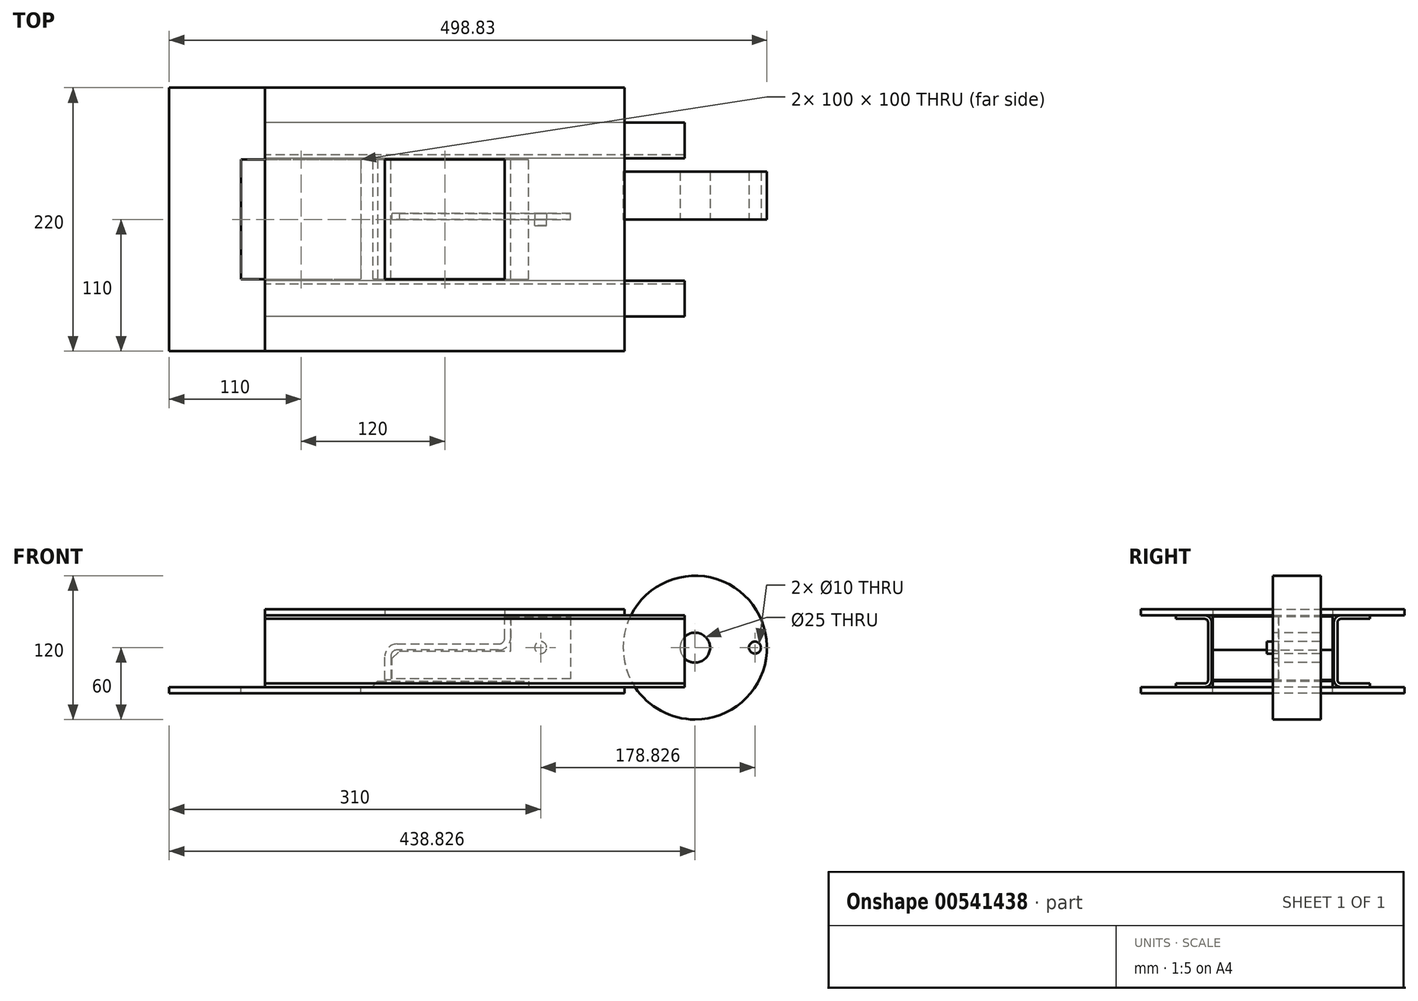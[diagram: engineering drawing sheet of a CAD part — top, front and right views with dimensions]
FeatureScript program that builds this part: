
annotation { "Feature Type Name" : "Feature", "Feature Type Description" : "" }
export const myFeature = defineFeature(function(context is Context, id is Id, definition is map)
    precondition{}
    {
        {
            var Q0;
            Q0=qCreatedBy(makeId("Top.planeOp"),FACE);
            var sketch = newSketch(context, id + "F0", { "sketchPlane" : qUnion([Q0])});
            skLineSegment(sketch, "E0.bottom", {"start": v(-50, -50) * mm, "end": v(50, -50) * mm});
            skLineSegment(sketch, "E0.top", {"start": v(-50, 50) * mm, "end": v(50, 50) * mm});
            skLineSegment(sketch, "E0.left", {"start": v(-50, -50) * mm, "end": v(-50, 50) * mm});
            skLineSegment(sketch, "E0.right", {"start": v(50, -50) * mm, "end": v(50, 50) * mm});
            skLineSegment(sketch, "E1.bottom", {"start": v(-150, -110) * mm, "end": v(150, -110) * mm});
            skLineSegment(sketch, "E1.top", {"start": v(-150, 110) * mm, "end": v(150, 110) * mm});
            skLineSegment(sketch, "E1.left", {"start": v(-150, -110) * mm, "end": v(-150, 110) * mm});
            skLineSegment(sketch, "E1.right", {"start": v(150, -110) * mm, "end": v(150, 110) * mm});
            skSolve(sketch);
        }
        {
            var Q0;
            Q0=makeQuery(id+"F0.imprint","IMPRINT",FACE,{"disambiguationData":[TD([[makeQuery(id+"F0.imprint","IMPRINT",EDGE,{"derivedFrom":sQuery(id+"F0.wireOp",EDGE,"E0.bottom")}),-1.0]])]});
            extrude(context, id + "F1", {"entities" : qUnion([Q0]), "depth" : 5 * mm, "offsetDistance" : 25 * mm});
        }
        {
            var Q0;
            Q0=makeQuery(id+"F1.opExtrude","CAP_FACE",FACE,{"disambiguationData":[OSD([sQuery(id+"F0.wireOp",EDGE,"E0.bottom"),sQuery(id+"F0.wireOp",EDGE,"E0.top"),sQuery(id+"F0.wireOp",EDGE,"E0.left"),sQuery(id+"F0.wireOp",EDGE,"E0.right"),sQuery(id+"F0.wireOp",EDGE,"E1.bottom"),sQuery(id+"F0.wireOp",EDGE,"E1.top"),sQuery(id+"F0.wireOp",EDGE,"E1.left"),sQuery(id+"F0.wireOp",EDGE,"E1.right")])],"isStart":true});
            cPlane(context, id + "F2", {"entities" : qUnion([Q0]), "cplaneType" : CPlaneType.OFFSET, "offset" : 60 * mm, "width" : 150 * mm, "height" : 150 * mm});
        }
        {
            var Q0;
            Q0=qCreatedBy(id+"F2.planeOp",FACE);
            var sketch = newSketch(context, id + "F3", { "sketchPlane" : qUnion([Q0])});
            skLineSegment(sketch, "E2.bottom", {"start": v(-170, -50) * mm, "end": v(-70, -50) * mm});
            skLineSegment(sketch, "E2.top", {"start": v(-170, 50) * mm, "end": v(-70, 50) * mm});
            skLineSegment(sketch, "E2.left", {"start": v(-170, -50) * mm, "end": v(-170, 50) * mm});
            skLineSegment(sketch, "E2.right", {"start": v(-70, -50) * mm, "end": v(-70, 50) * mm});
            skLineSegment(sketch, "E3.bottom", {"start": v(-230, -110) * mm, "end": v(150, -110) * mm});
            skLineSegment(sketch, "E3.top", {"start": v(-230, 110) * mm, "end": v(150, 110) * mm});
            skLineSegment(sketch, "E3.left", {"start": v(-230, -110) * mm, "end": v(-230, 110) * mm});
            skLineSegment(sketch, "E3.right", {"start": v(150, -110) * mm, "end": v(150, 110) * mm});
            skSolve(sketch);
        }
        {
            var Q0;
            Q0=makeQuery(id+"F3.imprint","IMPRINT",FACE,{"disambiguationData":[TD([[makeQuery(id+"F3.imprint","IMPRINT",EDGE,{"derivedFrom":sQuery(id+"F3.wireOp",EDGE,"E2.bottom")}),-1.0]])]});
            extrude(context, id + "F4", {"entities" : qUnion([Q0]), "depth" : 5 * mm, "offsetDistance" : 25 * mm});
        }
        {
            var Q0;
            Q0=qCreatedBy(makeId("Front.planeOp"),FACE);
            var sketch = newSketch(context, id + "F5", { "sketchPlane" : qUnion([Q0])});
            skLineSegment(sketch, "E4", {"start": v(-50, -54) * mm, "end": v(-50, -24) * mm});
            skLineSegment(sketch, "E5", {"start": v(-50, -24) * mm, "end": v(50, -24) * mm});
            skLineSegment(sketch, "E6", {"start": v(50, -24) * mm, "end": v(50, -1) * mm});
            skLineSegment(sketch, "E7", {"start": v(50, -1) * mm, "end": v(55, -1) * mm});
            skLineSegment(sketch, "E8", {"start": v(55, -1) * mm, "end": v(55, -29) * mm});
            skLineSegment(sketch, "E9", {"start": v(55, -29) * mm, "end": v(-45, -29) * mm});
            skLineSegment(sketch, "E10", {"start": v(-45, -29) * mm, "end": v(-45, -54) * mm});
            skLineSegment(sketch, "E11", {"start": v(-45, -54) * mm, "end": v(-50, -54) * mm});
            skSolve(sketch);
        }
        {
            var Q0;
            Q0=makeQuery(id+"F5.imprint","IMPRINT",FACE,{"disambiguationData":[TD([[makeQuery(id+"F5.imprint","IMPRINT",EDGE,{"derivedFrom":sQuery(id+"F5.wireOp",EDGE,"E4")}),-1.0]])]});
            extrude(context, id + "F6", {"entities" : qUnion([Q0]), "endBound" : BoundingType.SYMMETRIC, "depth" : 100 * mm, "offsetDistance" : 25 * mm});
        }
        {
            var Q0;
            Q0=makeQuery(id+"F6.opExtrude","SWEPT_EDGE",EDGE,{"disambiguationData":[OSD([sQuery(id+"F5.wireOp",EDGE,"E4"),sQuery(id+"F5.wireOp",EDGE,"E5")])]});
            var Q1;
            Q1=makeQuery(id+"F6.opExtrude","SWEPT_EDGE",EDGE,{"disambiguationData":[OSD([sQuery(id+"F5.wireOp",EDGE,"E8"),sQuery(id+"F5.wireOp",EDGE,"E9")])]});
            fillet(context, id + "F7", {"entities" : qUnion([Q0, Q1]), "radius" : 10 * mm, "tangentPropagation" : true, "allowEdgeOverflow" : false});
        }
        {
            var Q0;
            Q0=makeQuery(id+"F6.opExtrude","SWEPT_EDGE",EDGE,{"disambiguationData":[OSD([sQuery(id+"F5.wireOp",EDGE,"E9"),sQuery(id+"F5.wireOp",EDGE,"E10")])]});
            var Q1;
            Q1=makeQuery(id+"F6.opExtrude","SWEPT_EDGE",EDGE,{"disambiguationData":[OSD([sQuery(id+"F5.wireOp",EDGE,"E5"),sQuery(id+"F5.wireOp",EDGE,"E6")])]});
            fillet(context, id + "F8", {"entities" : qUnion([Q0, Q1]), "radius" : 5 * mm, "tangentPropagation" : true, "allowEdgeOverflow" : false});
        }
        {
            var Q0;
            Q0=qCreatedBy(id+"F2.planeOp",FACE);
            var sketch = newSketch(context, id + "F9", { "sketchPlane" : qUnion([Q0])});
            skLineSegment(sketch, "E12.bottom", {"start": v(-60, 50) * mm, "end": v(70, 50) * mm});
            skLineSegment(sketch, "E12.top", {"start": v(-60, -50) * mm, "end": v(70, -50) * mm});
            skLineSegment(sketch, "E12.left", {"start": v(-60, 50) * mm, "end": v(-60, -50) * mm});
            skLineSegment(sketch, "E12.right", {"start": v(70, 50) * mm, "end": v(70, -50) * mm});
            skSolve(sketch);
        }
        {
            var Q0;
            Q0=makeQuery(id+"F9.imprint","IMPRINT",FACE,{"disambiguationData":[TD([[makeQuery(id+"F9.imprint","IMPRINT",EDGE,{"derivedFrom":sQuery(id+"F9.wireOp",EDGE,"E12.bottom")}),-1.0]])]});
            extrude(context, id + "F10", {"entities" : qUnion([Q0]), "oppositeDirection" : true, "depth" : 5 * mm, "offsetDistance" : 25 * mm});
        }
        {
            var Q0;
            Q0=makeQuery(id+"F10.opExtrude","CAP_EDGE",EDGE,{"disambiguationData":[OSD([sQuery(id+"F9.wireOp",EDGE,"E12.left")])],"isStart":false});
            chamfer(context, id + "F11", {"entities" : qUnion([Q0]), "width" : 4 * mm, "tangentPropagation" : true});
        }
        {
            var Q0;
            Q0=qCreatedBy(makeId("Right.planeOp"),FACE);
            var sketch = newSketch(context, id + "F12", { "sketchPlane" : qUnion([Q0])});
            skLineSegment(sketch, "E13", {"start": v(-81, 0) * mm, "end": v(-51, 0) * mm});
            skLineSegment(sketch, "E14", {"start": v(-51, 0) * mm, "end": v(-51, -60) * mm});
            skLineSegment(sketch, "E15", {"start": v(-51, -60) * mm, "end": v(-81, -60) * mm});
            skLineSegment(sketch, "E16", {"start": v(-81, -60) * mm, "end": v(-81, -57) * mm});
            skLineSegment(sketch, "E17", {"start": v(-81, -57) * mm, "end": v(-54, -57) * mm});
            skLineSegment(sketch, "E18", {"start": v(-54, -57) * mm, "end": v(-54, -3) * mm});
            skLineSegment(sketch, "E19", {"start": v(-54, -3) * mm, "end": v(-81, -3) * mm});
            skLineSegment(sketch, "E20", {"start": v(-81, -3) * mm, "end": v(-81, 0) * mm});
            skSolve(sketch);
        }
        {
            var Q0;
            Q0=makeQuery(id+"F12.imprint","IMPRINT",FACE,{"disambiguationData":[TD([[makeQuery(id+"F12.imprint","IMPRINT",EDGE,{"derivedFrom":sQuery(id+"F12.wireOp",EDGE,"E13")}),-1.0]])]});
            extrude(context, id + "F13", {"entities" : qUnion([Q0]), "endBound" : BoundingType.SYMMETRIC, "depth" : 350 * mm, "offsetDistance" : 25 * mm});
        }
        {
            var Q0;
            Q0=makeQuery(id+"F13.opExtrude","SWEPT_BODY",BODY,{"disambiguationData":[OSD([sQuery(id+"F12.wireOp",EDGE,"E13"),sQuery(id+"F12.wireOp",EDGE,"E14"),sQuery(id+"F12.wireOp",EDGE,"E15"),sQuery(id+"F12.wireOp",EDGE,"E16"),sQuery(id+"F12.wireOp",EDGE,"E17"),sQuery(id+"F12.wireOp",EDGE,"E18"),sQuery(id+"F12.wireOp",EDGE,"E19"),sQuery(id+"F12.wireOp",EDGE,"E20")])]});
            var Q1;
            Q1=qCreatedBy(makeId("Front.planeOp"),FACE);
            mirror(context, id + "F14", {"entities" : qUnion([Q0]), "mirrorPlane" : qUnion([Q1])});
        }
        {
            var Q0;
            Q0=makeQuery(id+"F13.opExtrude","SWEPT_EDGE",EDGE,{"disambiguationData":[OSD([sQuery(id+"F12.wireOp",EDGE,"E18"),sQuery(id+"F12.wireOp",EDGE,"E19")])]});
            var Q1;
            Q1=makeQuery(id+"F13.opExtrude","SWEPT_EDGE",EDGE,{"disambiguationData":[OSD([sQuery(id+"F12.wireOp",EDGE,"E17"),sQuery(id+"F12.wireOp",EDGE,"E18")])]});
            var Q2;
            Q2=makeQuery(id+"F14.opPattern","COPY",EDGE,{"derivedFrom":makeQuery(id+"F13.opExtrude","SWEPT_EDGE",EDGE,{"disambiguationData":[OSD([sQuery(id+"F12.wireOp",EDGE,"E17"),sQuery(id+"F12.wireOp",EDGE,"E18")])]}),"instanceName":"1"});
            var Q3;
            Q3=makeQuery(id+"F14.opPattern","COPY",EDGE,{"derivedFrom":makeQuery(id+"F13.opExtrude","SWEPT_EDGE",EDGE,{"disambiguationData":[OSD([sQuery(id+"F12.wireOp",EDGE,"E18"),sQuery(id+"F12.wireOp",EDGE,"E19")])]}),"instanceName":"1"});
            fillet(context, id + "F15", {"entities" : qUnion([Q0, Q1, Q2, Q3]), "radius" : 3 * mm, "tangentPropagation" : true, "allowEdgeOverflow" : false});
        }
        {
            var Q0;
            Q0=makeQuery(id+"F13.opExtrude","SWEPT_EDGE",EDGE,{"disambiguationData":[OSD([sQuery(id+"F12.wireOp",EDGE,"E13"),sQuery(id+"F12.wireOp",EDGE,"E14")])]});
            var Q1;
            Q1=makeQuery(id+"F13.opExtrude","SWEPT_EDGE",EDGE,{"disambiguationData":[OSD([sQuery(id+"F12.wireOp",EDGE,"E14"),sQuery(id+"F12.wireOp",EDGE,"E15")])]});
            var Q2;
            Q2=makeQuery(id+"F14.opPattern","COPY",EDGE,{"derivedFrom":makeQuery(id+"F13.opExtrude","SWEPT_EDGE",EDGE,{"disambiguationData":[OSD([sQuery(id+"F12.wireOp",EDGE,"E13"),sQuery(id+"F12.wireOp",EDGE,"E14")])]}),"instanceName":"1"});
            var Q3;
            Q3=makeQuery(id+"F14.opPattern","COPY",EDGE,{"derivedFrom":makeQuery(id+"F13.opExtrude","SWEPT_EDGE",EDGE,{"disambiguationData":[OSD([sQuery(id+"F12.wireOp",EDGE,"E14"),sQuery(id+"F12.wireOp",EDGE,"E15")])]}),"instanceName":"1"});
            fillet(context, id + "F16", {"entities" : qUnion([Q0, Q1, Q2, Q3]), "radius" : 6 * mm, "tangentPropagation" : true, "allowEdgeOverflow" : false});
        }
        {
            var Q0;
            Q0=makeQuery(id+"F14.opPattern","COPY",BODY,{"derivedFrom":makeQuery(id+"F13.opExtrude","SWEPT_BODY",BODY,{"disambiguationData":[OSD([sQuery(id+"F12.wireOp",EDGE,"E13"),sQuery(id+"F12.wireOp",EDGE,"E14"),sQuery(id+"F12.wireOp",EDGE,"E15"),sQuery(id+"F12.wireOp",EDGE,"E16"),sQuery(id+"F12.wireOp",EDGE,"E17"),sQuery(id+"F12.wireOp",EDGE,"E18"),sQuery(id+"F12.wireOp",EDGE,"E19"),sQuery(id+"F12.wireOp",EDGE,"E20")])]}),"instanceName":"1"});
            var Q1;
            Q1=makeQuery(id+"F13.opExtrude","SWEPT_BODY",BODY,{"disambiguationData":[OSD([sQuery(id+"F12.wireOp",EDGE,"E13"),sQuery(id+"F12.wireOp",EDGE,"E14"),sQuery(id+"F12.wireOp",EDGE,"E15"),sQuery(id+"F12.wireOp",EDGE,"E16"),sQuery(id+"F12.wireOp",EDGE,"E17"),sQuery(id+"F12.wireOp",EDGE,"E18"),sQuery(id+"F12.wireOp",EDGE,"E19"),sQuery(id+"F12.wireOp",EDGE,"E20")])]});
            var Q2;
            Q2=makeQuery(id+"F13.opExtrude","SWEPT_EDGE",EDGE,{"disambiguationData":[OSD([sQuery(id+"F12.wireOp",EDGE,"E13"),sQuery(id+"F12.wireOp",EDGE,"E20")])]});
            transform(context, id + "F17", {"entities" : qUnion([Q0, Q1]), "transformType" : TransformType.TRANSLATION_DISTANCE, "transformDirection" : qUnion([Q2]), "distance" : 25 * mm, "oppositeDirection" : true, "makeCopy" : false});
        }
        {
            var Q0;
            Q0=qCreatedBy(makeId("Front.planeOp"),FACE);
            var sketch = newSketch(context, id + "F18", { "sketchPlane" : qUnion([Q0])});
            skLineSegment(sketch, "E21", {"start": v(-44, -30) * mm, "end": v(55, -30) * mm});
            skLineSegment(sketch, "E22", {"start": v(55, -30) * mm, "end": v(55, -1) * mm});
            skLineSegment(sketch, "E23", {"start": v(55, -1) * mm, "end": v(105, -1) * mm});
            skLineSegment(sketch, "E24", {"start": v(105, -1) * mm, "end": v(105, -53) * mm});
            skLineSegment(sketch, "E25", {"start": v(105, -53) * mm, "end": v(-44, -53) * mm});
            skLineSegment(sketch, "E26", {"start": v(-44, -53) * mm, "end": v(-44, -30) * mm});
            skSolve(sketch);
        }
        {
            var Q0;
            Q0=makeQuery(id+"F18.imprint","IMPRINT",FACE,{"disambiguationData":[TD([[makeQuery(id+"F18.imprint","IMPRINT",EDGE,{"derivedFrom":sQuery(id+"F18.wireOp",EDGE,"E21")}),-1.0]])]});
            extrude(context, id + "F19", {"entities" : qUnion([Q0]), "endBound" : BoundingType.SYMMETRIC, "depth" : 5 * mm, "offsetDistance" : 25 * mm});
        }
        {
            var Q0;
            Q0=makeQuery(id+"F19.opExtrude","SWEPT_BODY",BODY,{"disambiguationData":[OSD([sQuery(id+"F18.wireOp",EDGE,"E21"),sQuery(id+"F18.wireOp",EDGE,"E22"),sQuery(id+"F18.wireOp",EDGE,"E23"),sQuery(id+"F18.wireOp",EDGE,"E24"),sQuery(id+"F18.wireOp",EDGE,"E25"),sQuery(id+"F18.wireOp",EDGE,"E26")])]});
            var Q1;
            Q1=makeQuery(id+"F19.opExtrude","SWEPT_EDGE",EDGE,{"disambiguationData":[OSD([sQuery(id+"F18.wireOp",EDGE,"E23"),sQuery(id+"F18.wireOp",EDGE,"E24")])]});
            transform(context, id + "F20", {"entities" : qUnion([Q0]), "transformType" : TransformType.TRANSLATION_DISTANCE, "transformDirection" : qUnion([Q1]), "distance" : 2.5 * mm, "makeCopy" : false});
        }
        {
            var Q0;
            Q0=makeQuery(id+"F19.opExtrude","CAP_FACE",FACE,{"disambiguationData":[OSD([sQuery(id+"F18.wireOp",EDGE,"E21"),sQuery(id+"F18.wireOp",EDGE,"E22"),sQuery(id+"F18.wireOp",EDGE,"E23"),sQuery(id+"F18.wireOp",EDGE,"E24"),sQuery(id+"F18.wireOp",EDGE,"E25"),sQuery(id+"F18.wireOp",EDGE,"E26")])],"isStart":false});
            var sketch = newSketch(context, id + "F21", { "sketchPlane" : qUnion([Q0])});
            skPoint(sketch, "E27", {"position": v(80, -27) * mm});
            skLineSegment(sketch, "E28", {"start": v(105, -27) * mm, "end": v(80, -27) * mm});
            skSolve(sketch);
        }
        {
            var Q0;
            Q0=sQuery(id+"F21.wireOp",VERTEX,"E27");
            var Q1;
            Q1=makeQuery(id+"F19.opExtrude","SWEPT_BODY",BODY,{"disambiguationData":[OSD([sQuery(id+"F18.wireOp",EDGE,"E21"),sQuery(id+"F18.wireOp",EDGE,"E22"),sQuery(id+"F18.wireOp",EDGE,"E23"),sQuery(id+"F18.wireOp",EDGE,"E24"),sQuery(id+"F18.wireOp",EDGE,"E25"),sQuery(id+"F18.wireOp",EDGE,"E26")])]});
            hole(context, id + "F22", {"style" : HoleStyle.SIMPLE, "endStyle" : HoleEndStyle.BLIND, "holeDiameter" : 10 * mm, "holeDepth" : 10 * mm, "isTappedThrough" : true, "tappedDepth" : 12 * mm, "tapClearance" : 3, "locations" : qUnion([Q0]), "scope" : qUnion([Q1])});
        }
        {
            var Q0;
            Q0=makeQuery(id+"F19.opExtrude","SWEPT_EDGE",EDGE,{"disambiguationData":[OSD([sQuery(id+"F18.wireOp",EDGE,"E21"),sQuery(id+"F18.wireOp",EDGE,"E26")])]});
            chamfer(context, id + "F23", {"entities" : qUnion([Q0]), "width" : 6 * mm, "tangentPropagation" : true});
        }
        {
            var Q0;
            Q0=makeQuery(id+"F19.opExtrude","CAP_FACE",FACE,{"disambiguationData":[OSD([sQuery(id+"F18.wireOp",EDGE,"E21"),sQuery(id+"F18.wireOp",EDGE,"E22"),sQuery(id+"F18.wireOp",EDGE,"E23"),sQuery(id+"F18.wireOp",EDGE,"E24"),sQuery(id+"F18.wireOp",EDGE,"E25"),sQuery(id+"F18.wireOp",EDGE,"E26")])],"isStart":false});
            var sketch = newSketch(context, id + "F24", { "sketchPlane" : qUnion([Q0])});
            skCircle(sketch, "E29", {"center": v(223.83, -27) * mm, "radius": 60 * mm});
            skPoint(sketch, "E29.centerSnap0", {"position": v(105, -27) * mm});
            skCircle(sketch, "E30", {"center": v(223.83, -27) * mm, "radius": 12.5 * mm});
            skSolve(sketch);
        }
        {
            var Q0;
            Q0=makeQuery(id+"F24.imprint","IMPRINT",FACE,{"disambiguationData":[TD([[makeQuery(id+"F24.imprint","IMPRINT",EDGE,{"derivedFrom":sQuery(id+"F24.wireOp",EDGE,"E29")}),1.0]])]});
            extrude(context, id + "F25", {"entities" : qUnion([Q0]), "oppositeDirection" : true, "depth" : 40 * mm, "offsetDistance" : 25 * mm});
        }
        {
            var Q0;
            Q0=makeQuery(id+"F25.opExtrude","CAP_FACE",FACE,{"disambiguationData":[OSD([sQuery(id+"F24.wireOp",EDGE,"E29"),sQuery(id+"F24.wireOp",EDGE,"E30")])],"isStart":true});
            var sketch = newSketch(context, id + "F26", { "sketchPlane" : qUnion([Q0])});
            skPoint(sketch, "E31", {"position": v(273.83, -27) * mm});
            skLineSegment(sketch, "E32", {"start": v(273.83, -27) * mm, "end": v(223.83, -27) * mm});
            skSolve(sketch);
        }
        {
            var Q0;
            Q0=sQuery(id+"F26.wireOp",VERTEX,"E31");
            var Q1;
            Q1=makeQuery(id+"F25.opExtrude","SWEPT_BODY",BODY,{"disambiguationData":[OSD([sQuery(id+"F24.wireOp",EDGE,"E29"),sQuery(id+"F24.wireOp",EDGE,"E30")])]});
            hole(context, id + "F27", {"style" : HoleStyle.SIMPLE, "endStyle" : HoleEndStyle.THROUGH, "holeDiameter" : 10 * mm, "isTappedThrough" : true, "tappedDepth" : 12 * mm, "tapClearance" : 3, "locations" : qUnion([Q0]), "scope" : qUnion([Q1])});
        }
        {
            var Q0;
            Q0=makeQuery(id+"F25.opExtrude","SWEPT_BODY",BODY,{"disambiguationData":[OSD([sQuery(id+"F24.wireOp",EDGE,"E29"),sQuery(id+"F24.wireOp",EDGE,"E30")])]});
            var Q1;
            {var subQ0=sQuery(id+"F12.wireOp",EDGE,"E18");Q1=makeQuery(id+"F15.opFillet","BLEND_EDGE",EDGE,{"blendedFrom":[makeQuery(id+"F13.opExtrude","SWEPT_EDGE",EDGE,{"disambiguationData":[OSD([sQuery(id+"F12.wireOp",EDGE,"E17"),subQ0])]}),makeQuery(id+"F13.opExtrude","SWEPT_FACE",FACE,{"disambiguationData":[OSD([subQ0])]})],"blendedInto":[makeQuery(id+"F13.opExtrude","SWEPT_FACE",FACE,{"disambiguationData":[OSD([subQ0])]})]});}
            transform(context, id + "F28", {"entities" : qUnion([Q0]), "transformType" : TransformType.TRANSLATION_DISTANCE, "transformDirection" : qUnion([Q1]), "distance" : 15 * mm, "oppositeDirection" : true, "makeCopy" : false});
        }
        {
            var Q0;
            Q0=qCreatedBy(makeId("Front.planeOp"),FACE);
            var sketch = newSketch(context, id + "F29", { "sketchPlane" : qUnion([Q0])});
            skCircle(sketch, "E33", {"center": v(80, -27) * mm, "radius": 5 * mm});
            skCircle(sketch, "E34", {"center": v(258.83, -27) * mm, "radius": 5 * mm});
            skLineSegment(sketch, "E35", {"start": v(80, -27) * mm, "end": v(243.83, -27) * mm});
            skArc(sketch, "E36.0", {"start": v(91.18, -37) * mm, "mid": v(65, -27) * mm, "end": v(91.18, -17) * mm});
            skArc(sketch, "E37.0", {"start": v(247.65, -17) * mm, "mid": v(273.83, -27) * mm, "end": v(247.65, -37) * mm});
            skLineSegment(sketch, "E38", {"start": v(91.18, -17) * mm, "end": v(247.65, -17) * mm});
            skLineSegment(sketch, "E39", {"start": v(91.18, -37) * mm, "end": v(247.65, -37) * mm});
            skSolve(sketch);
        }
        {
            var Q0;
            Q0=makeQuery(id+"F29.imprint","IMPRINT",FACE,{"disambiguationData":[TD([[makeQuery(id+"F29.imprint","IMPRINT",EDGE,{"derivedFrom":sQuery(id+"F29.wireOp",EDGE,"E33")}),1.0]])]});
            extrude(context, id + "F30", {"entities" : qUnion([Q0]), "depth" : 5 * mm, "offsetDistance" : 25 * mm});
        }
    });
